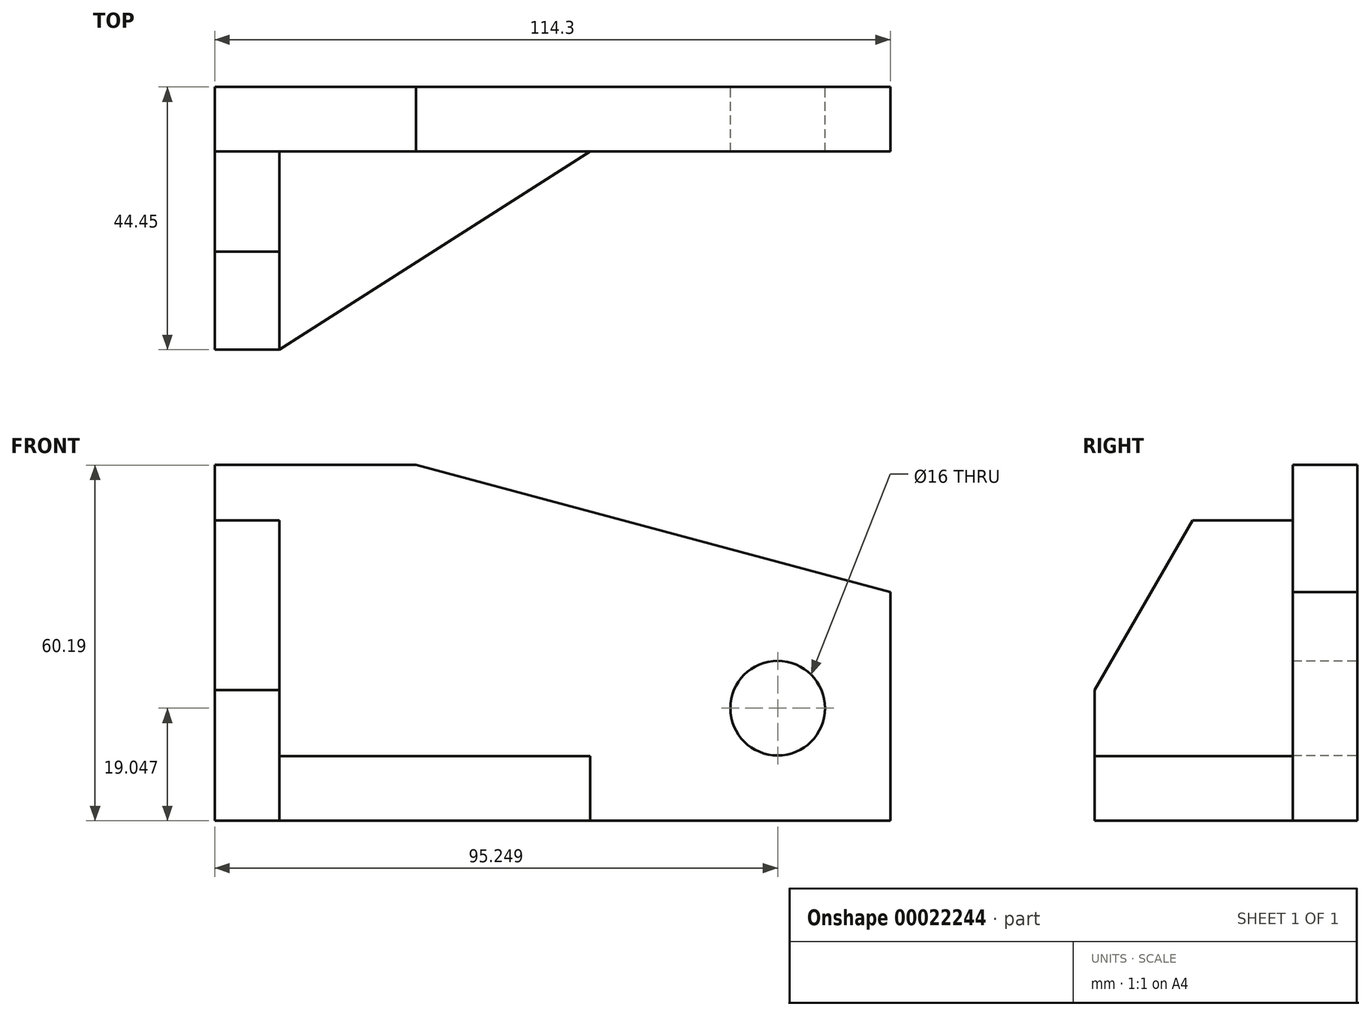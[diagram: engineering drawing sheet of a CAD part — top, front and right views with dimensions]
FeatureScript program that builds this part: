
annotation { "Feature Type Name" : "Feature", "Feature Type Description" : "" }
export const myFeature = defineFeature(function(context is Context, id is Id, definition is map)
    precondition{}
    {
        {
            var Q0;
            Q0=qCreatedBy(makeId("Front.planeOp"),FACE);
            var sketch = newSketch(context, id + "F0", { "sketchPlane" : qUnion([Q0])});
            skLineSegment(sketch, "E0.bottom", {"start": v(-56.81, 33.37) * mm, "end": v(57.49, 33.37) * mm});
            skLineSegment(sketch, "E0.top", {"start": v(-56.81, -26.82) * mm, "end": v(57.49, -26.82) * mm});
            skLineSegment(sketch, "E0.left", {"start": v(-56.81, 33.37) * mm, "end": v(-56.81, -26.82) * mm});
            skLineSegment(sketch, "E0.right", {"start": v(57.49, 33.37) * mm, "end": v(57.49, -26.82) * mm});
            skCircle(sketch, "E1", {"center": v(38.44, -7.77) * mm, "radius": 8 * mm});
            skLineSegment(sketch, "E2", {"start": v(-22.73, 33.37) * mm, "end": v(57.49, 11.88) * mm});
            skSolve(sketch);
        }
        {
            var Q0;
            {var subQ2=sQuery(id+"F0.wireOp",EDGE,"E0.top");Q0=makeQuery(id+"F0.imprint","IMPRINT",FACE,{"disambiguationData":[TD([[makeQuery(id+"F0.imprint","IMPRINT",EDGE,{"derivedFrom":subQ2}),1.0]])]});}
            extrude(context, id + "F1", {"entities" : qUnion([Q0]), "depth" : 10.92 * mm});
        }
        {
            var Q0;
            Q0=makeQuery(id+"F1.opExtrude","SWEPT_FACE",FACE,{"disambiguationData":[OSD([sQuery(id+"F0.wireOp",EDGE,"E0.left")])]});
            var sketch = newSketch(context, id + "F2", { "sketchPlane" : qUnion([Q0])});
            skLineSegment(sketch, "E3.bottom", {"start": v(0, -26.82) * mm, "end": v(44.45, -26.82) * mm});
            skLineSegment(sketch, "E3.top", {"start": v(0, 23.98) * mm, "end": v(44.45, 23.98) * mm});
            skLineSegment(sketch, "E3.left", {"start": v(0, -26.82) * mm, "end": v(0, 23.98) * mm});
            skLineSegment(sketch, "E3.right", {"start": v(44.45, -26.82) * mm, "end": v(44.45, 23.98) * mm});
            skLineSegment(sketch, "E4", {"start": v(44.45, -4.73) * mm, "end": v(27.88, 23.98) * mm});
            skSolve(sketch);
        }
        {
            var Q0;
            {var subQ5=sQuery(id+"F2.wireOp",EDGE,"E4");Q0=makeQuery(id+"F2.imprint","IMPRINT",FACE,{"disambiguationData":[TD([[makeQuery(id+"F2.imprint","IMPRINT",EDGE,{"derivedFrom":subQ5}),1.0]])]});}
            var Q1;
            {var subQ6=sQuery(id+"F2.wireOp",EDGE,"E3.left");Q1=makeQuery(id+"F2.imprint","IMPRINT",FACE,{"disambiguationData":[TD([[makeQuery(id+"F2.imprint","IMPRINT",EDGE,{"derivedFrom":subQ6}),1.0]])]});}
            extrude(context, id + "F3", {"entities" : qUnion([Q0, Q1]), "operationType" : NewBodyOperationType.ADD, "oppositeDirection" : true, "depth" : 10.92 * mm});
        }
        {
            var Q0;
            Q0=makeQuery(id+"F3.boolean.opBoolean","MERGE",FACE,{"derivedFrom":[makeQuery(id+"F1.opExtrude","SWEPT_FACE",FACE,{"disambiguationData":[OSD([sQuery(id+"F0.wireOp",EDGE,"E0.top")])]}),makeQuery(id+"F3.opExtrude","SWEPT_FACE",FACE,{"disambiguationData":[OSD([sQuery(id+"F2.wireOp",EDGE,"E3.bottom")])]})]});
            var sketch = newSketch(context, id + "F4", { "sketchPlane" : qUnion([Q0])});
            skLineSegment(sketch, "E5.bottom", {"start": v(-56.81, 0) * mm, "end": v(6.69, 0) * mm});
            skLineSegment(sketch, "E5.top", {"start": v(-56.81, 44.45) * mm, "end": v(6.69, 44.45) * mm});
            skLineSegment(sketch, "E5.left", {"start": v(-56.81, 0) * mm, "end": v(-56.81, 44.45) * mm});
            skLineSegment(sketch, "E5.right", {"start": v(6.69, 0) * mm, "end": v(6.69, 44.45) * mm});
            skLineSegment(sketch, "E6", {"start": v(-45.89, 44.45) * mm, "end": v(6.69, 10.92) * mm});
            skSolve(sketch);
        }
        {
            var Q0;
            {var subQ6=sQuery(id+"F4.wireOp",EDGE,"E5.bottom");Q0=makeQuery(id+"F4.imprint","IMPRINT",FACE,{"disambiguationData":[TD([[makeQuery(id+"F4.imprint","IMPRINT",EDGE,{"derivedFrom":subQ6}),1.0]])]});}
            var Q1;
            {var subQ1=sQuery(id+"F4.wireOp",EDGE,"E6");Q1=makeQuery(id+"F4.imprint","IMPRINT",FACE,{"disambiguationData":[TD([[makeQuery(id+"F4.imprint","IMPRINT",EDGE,{"derivedFrom":subQ1}),-1.0]])]});}
            extrude(context, id + "F5", {"entities" : qUnion([Q0, Q1]), "operationType" : NewBodyOperationType.ADD, "oppositeDirection" : true, "depth" : 10.92 * mm});
        }
    });
